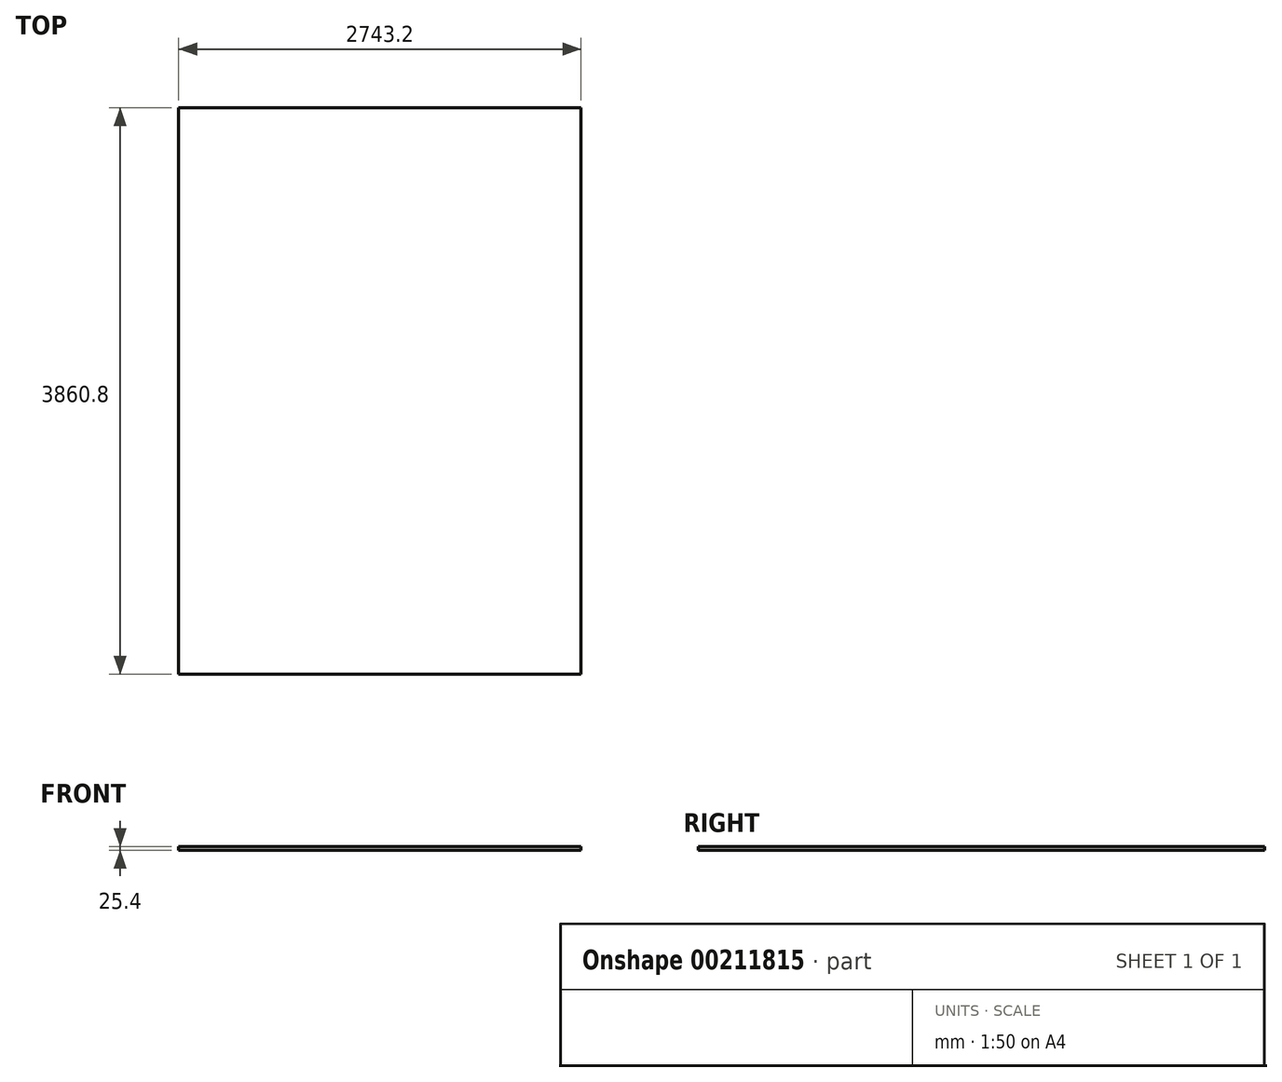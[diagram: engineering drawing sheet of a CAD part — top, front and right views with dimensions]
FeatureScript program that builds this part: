
annotation { "Feature Type Name" : "Feature", "Feature Type Description" : "" }
export const myFeature = defineFeature(function(context is Context, id is Id, definition is map)
    precondition{}
    {
        {
            var Q0;
            Q0=qCreatedBy(makeId("Top.planeOp"),FACE);
            var sketch = newSketch(context, id + "F0", { "sketchPlane" : qUnion([Q0])});
            skLineSegment(sketch, "E0.bottom", {"start": v(0, 0) * mm, "end": v(2743.2, 0) * mm});
            skLineSegment(sketch, "E0.top", {"start": v(0, 3860.8) * mm, "end": v(2743.2, 3860.8) * mm});
            skLineSegment(sketch, "E0.left", {"start": v(0, 0) * mm, "end": v(0, 3860.8) * mm});
            skLineSegment(sketch, "E0.right", {"start": v(2743.2, 0) * mm, "end": v(2743.2, 3860.8) * mm});
            skSolve(sketch);
        }
        {
            var Q0;
            Q0 = qSketchRegion(id + "F0", true);
            extrude(context, id + "F1", {"entities" : qUnion([Q0]), "depth" : 25.4 * mm});
        }
    });
